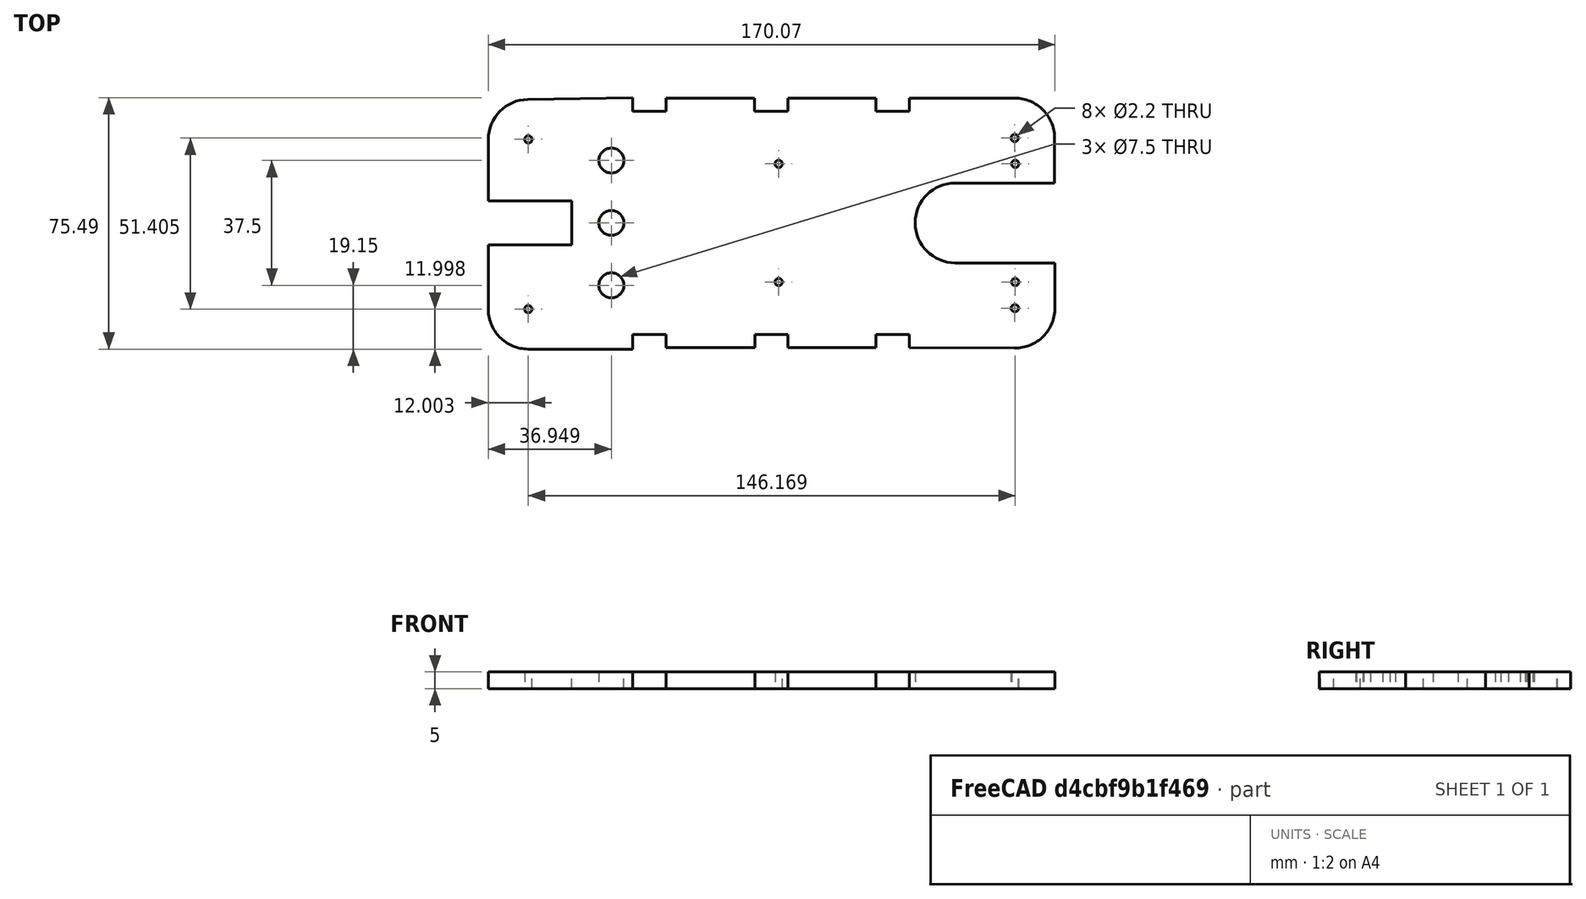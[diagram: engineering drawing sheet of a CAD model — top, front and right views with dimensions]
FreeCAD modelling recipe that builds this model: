
FCSTD DOCUMENT  (FreeCAD 1.0R38643 (Git))
Label: Acryl04
License: All rights reserved
LicenseURL: https://en.wikipedia.org/wiki/All_rights_reserved
objects: TechDraw::DrawViewDimension×26, Sketcher::SketchObject×1, PartDesign::Pad×1, PartDesign::Body×1, TechDraw::DrawSVGTemplate×1, TechDraw::DrawProjGroupItem×1, TechDraw::DrawPage×1
note: 51 computed .brp shape members not serialized (recipe doc carries the construction recipe); baked Part::Feature solids carry a one-line shape summary decoded from their .brp

FEATURE [Sketcher::SketchObject] Sketch
  ArcFitTolerance = 1e-06
  AttachmentSupport = -> [XY_Plane]
  FullyConstrained = false
  MakeInternals = false
  MapMode = 5
  sketch-geometry (59):
    g0: LineSegment StartX=-152.2 StartY=62.599 StartZ=0 EndX=-152.2 EndY=44.0923 EndZ=0
    g1: LineSegment StartX=-140.207 StartY=-0.401585 StartZ=0 EndX=-108.827 EndY=-0.401585 EndZ=0
    g2: LineSegment StartX=5.80682 StartY=75.0036 StartZ=0 EndX=-25.8266 EndY=75.0036 EndZ=0
    g3: ArcOfCircle CenterX=-140.2 CenterY=62.599 CenterZ=0 NormalX=0 NormalY=0 NormalZ=1 AngleXU=0 Radius=12 StartAngle=1.58146 EndAngle=3.14159
    g4: ArcOfCircle CenterX=-140.207 CenterY=11.5984 CenterZ=0 NormalX=0 NormalY=0 NormalZ=1 AngleXU=0 Radius=12 StartAngle=3.10801 EndAngle=4.71239
    g5: ArcOfCircle CenterX=5.86058 CenterY=11.8821 CenterZ=0 NormalX=0 NormalY=0 NormalZ=1 AngleXU=0 Radius=12 StartAngle=4.71296 EndAngle=6.29301
    g6: ArcOfCircle CenterX=5.80682 CenterY=63.0036 CenterZ=0 NormalX=0 NormalY=0 NormalZ=1 AngleXU=0 Radius=12 StartAngle=6.24947 EndAngle=7.85398
    g7: GeomPoint [constr] X=-152.2 Y=74.4139 Z=0
    g8: Circle CenterX=5.96219 CenterY=55.25 CenterZ=0 NormalX=0 NormalY=0 NormalZ=1 AngleXU=0 Radius=1.1
    g9: Circle CenterX=-65.0378 CenterY=55.25 CenterZ=0 NormalX=0 NormalY=0 NormalZ=1 AngleXU=0 Radius=1.1
    g10: Circle CenterX=-65.0378 CenterY=19.75 CenterZ=0 NormalX=0 NormalY=0 NormalZ=1 AngleXU=0 Radius=1.1
    g11: Circle CenterX=5.96219 CenterY=19.75 CenterZ=0 NormalX=0 NormalY=0 NormalZ=1 AngleXU=0 Radius=1.1
    g12: ArcOfCircle CenterX=-12.05 CenterY=37.5 CenterZ=0 NormalX=0 NormalY=0 NormalZ=1 AngleXU=0 Radius=12 StartAngle=1.5708 EndAngle=4.71239
    g13: LineSegment StartX=17.86 StartY=25.5 StartZ=0 EndX=-12.05 EndY=25.5 EndZ=0
    g14: LineSegment StartX=17.8 StartY=49.5 StartZ=0 EndX=-12.05 EndY=49.5 EndZ=0
    g15: GeomPoint X=17.8 Y=49.5 Z=0
    g16: GeomPoint X=17.86 Y=25.5 Z=0
    g17: LineSegment StartX=17.86 StartY=25.5 StartZ=0 EndX=17.86 EndY=12 EndZ=0
    g18: LineSegment StartX=17.8 StartY=49.5 StartZ=0 EndX=17.8 EndY=62.599 EndZ=0
    g19: Circle CenterX=-140.2 CenterY=62.599 CenterZ=0 NormalX=0 NormalY=0 NormalZ=1 AngleXU=0 Radius=1.1
    g20: Circle CenterX=-140.207 CenterY=11.5984 CenterZ=0 NormalX=0 NormalY=0 NormalZ=1 AngleXU=0 Radius=1.1
    g21: Circle CenterX=5.86058 CenterY=11.8821 CenterZ=0 NormalX=0 NormalY=0 NormalZ=1 AngleXU=0 Radius=1.1
    g22: Circle CenterX=5.80682 CenterY=63.0036 CenterZ=0 NormalX=0 NormalY=0 NormalZ=1 AngleXU=0 Radius=1.1
    g23: GeomPoint X=-115.261 Y=37.5 Z=0
    g24: Circle CenterX=-115.261 CenterY=37.5 CenterZ=0 NormalX=0 NormalY=0 NormalZ=1 AngleXU=0 Radius=3.75
    g25: Circle CenterX=-115.261 CenterY=56.25 CenterZ=0 NormalX=0 NormalY=0 NormalZ=1 AngleXU=0 Radius=3.75
    g26: GeomPoint X=-110.295 Y=56.25 Z=0
    g27: GeomPoint X=-115.261 Y=56.25 Z=0
    g28: Circle CenterX=-115.261 CenterY=18.75 CenterZ=0 NormalX=0 NormalY=0 NormalZ=1 AngleXU=0 Radius=3.75
    g29: GeomPoint X=-115.261 Y=18.75 Z=0
    g30: LineSegment StartX=-108.82 StartY=71.0877 StartZ=0 EndX=-98.82 EndY=71.0877 EndZ=0
    g31: LineSegment StartX=-72.3266 StartY=71 StartZ=0 EndX=-62.3266 EndY=71 EndZ=0
    g32: LineSegment StartX=-62.3266 StartY=71 StartZ=0 EndX=-62.3266 EndY=75 EndZ=0
    g33: LineSegment StartX=-72.3266 StartY=75 StartZ=0 EndX=-72.3266 EndY=71 EndZ=0
    g34: LineSegment StartX=-35.8266 StartY=71 StartZ=0 EndX=-25.8266 EndY=71 EndZ=0
    g35: LineSegment StartX=-25.8266 StartY=71 StartZ=0 EndX=-25.8266 EndY=75.0036 EndZ=0
    g36: LineSegment StartX=-35.8266 StartY=75 StartZ=0 EndX=-35.8266 EndY=71 EndZ=0
    g37: GeomPoint X=-108.82 Y=75.0877 Z=0
    g38: LineSegment StartX=-108.82 StartY=75.0877 StartZ=0 EndX=-108.82 EndY=71.0877 EndZ=0
    g39: LineSegment StartX=-98.82 StartY=71.0877 StartZ=0 EndX=-98.82 EndY=75 EndZ=0
    g40: LineSegment StartX=-108.82 StartY=75.0877 StartZ=0 EndX=-140.328 EndY=74.5983 EndZ=0
    g41: LineSegment StartX=-72.3266 StartY=75 StartZ=0 EndX=-98.82 EndY=75 EndZ=0
    g42: LineSegment StartX=-35.8266 StartY=75 StartZ=0 EndX=-62.3266 EndY=75 EndZ=0
    g43: LineSegment StartX=-98.8266 StartY=0 StartZ=0 EndX=-98.8266 EndY=4 EndZ=0
    g44: LineSegment StartX=-98.8266 StartY=4 StartZ=0 EndX=-108.827 EndY=4 EndZ=0
    g45: LineSegment StartX=-108.827 StartY=4 StartZ=0 EndX=-108.827 EndY=-0.401585 EndZ=0
    g46: LineSegment StartX=-62.2333 StartY=0 StartZ=0 EndX=-62.2333 EndY=4 EndZ=0
    g47: LineSegment StartX=-62.2333 StartY=4 StartZ=0 EndX=-72.2333 EndY=4 EndZ=0
    g48: LineSegment StartX=-72.2333 StartY=4 StartZ=0 EndX=-72.2333 EndY=0 EndZ=0
    g49: LineSegment StartX=-25.8266 StartY=0 StartZ=0 EndX=-25.8266 EndY=4 EndZ=0
    g50: LineSegment StartX=-25.8266 StartY=4 StartZ=0 EndX=-35.8266 EndY=4 EndZ=0
    g51: LineSegment StartX=-35.8266 StartY=4 StartZ=0 EndX=-35.8266 EndY=4e-16 EndZ=0
    g52: LineSegment StartX=-62.2333 StartY=0 StartZ=0 EndX=-35.8266 EndY=5e-16 EndZ=0
    g53: LineSegment StartX=-98.8266 StartY=0 StartZ=0 EndX=-72.2333 EndY=0 EndZ=0
    g54: LineSegment StartX=-25.8266 StartY=0 StartZ=0 EndX=5.86745 EndY=-0.117862 EndZ=0
    g55: LineSegment StartX=-152.2 StartY=30.8923 StartZ=0 EndX=-127.2 EndY=30.8923 EndZ=0
    g56: LineSegment StartX=-127.2 StartY=30.8923 StartZ=0 EndX=-127.2 EndY=44.0923 EndZ=0
    g57: LineSegment StartX=-127.2 StartY=44.0923 StartZ=0 EndX=-152.2 EndY=44.0923 EndZ=0
    g58: LineSegment StartX=-152.2 StartY=30.8923 StartZ=0 EndX=-152.2 EndY=12.0013 EndZ=0
  constraints (120):
    c: Tangent(g0,g3) = -1.5708
    c: Coincident(g58,g4) = -1.5708
    c: Tangent(g1,g4) = -1.5708
    c: Coincident(g54,g5) = -1.5708
    c: Tangent(g2,g6) = -1.5708
    c: Coincident(g40,g3) = -1.5708
    c: Vertical(g0)
    c: Horizontal(g1)
    c: Horizontal(g2)
    c: Equal(g3,g4)
    c: Equal(g4,g5)
    c: Equal(g5,g6)
    c: PointOnObject(g7,g0)
    c: PointOnObject(g7,g40)
    c: Distance(g0,g6) = 170
    c: Distance(g1,g40) = 75
    c: Radius(g4) = 12
    c: Diameter(g8) = 2.2
    c: Diameter(g9) = 2.2
    c: Horizontal(g8,g9)
    c: DistanceX(g9,g8) = 71
    c: Diameter(g10) = 2.2
    c: Diameter(g11) = 2.2
    c: Vertical(g10,g9)
    c: Vertical(g11,g8)
    c: Horizontal(g10,g11)
    c: DistanceY(g10,g9) = 35.5
    c: Tangent(g12,g13) = 1.5708
    c: Tangent(g12,g14) = -1.5708
    c: Angle(g-1,g13) = 3.14159
    c: Coincident(g15,g14)
    c: Coincident(g16,g13)
    c: Coincident(g17,g13)
    c: Vertical(g17)
    c: Coincident(g18,g14)
    c: Vertical(g18)
    c: Diameter(g19) = 2.2
    c: Coincident(g19,g3)
    c: Diameter(g20) = 2.2
    c: Coincident(g20,g4)
    c: Diameter(g21) = 2.2
    c: Coincident(g21,g5)
    c: Diameter(g22) = 2.2
    c: Coincident(g22,g6)
    c: Diameter(g24) = 7.5
    c: Coincident(g24,g23)
    c: Diameter(g25) = 7.5
    c: Coincident(g25,g27)
    c: Diameter(g28) = 7.5
    c: Coincident(g29,g28)
    c: Horizontal(g30)
    c: Distance(g30,g30) = 10
    c: Coincident(g31,g32)
    c: Coincident(g33,g31)
    c: Horizontal(g31)
    c: Vertical(g32)
    c: Vertical(g33)
    c: Distance(g32,g33) = 10
    c: Coincident(g34,g35)
    c: Coincident(g36,g34)
    c: Horizontal(g34)
    c: Vertical(g35)
    c: Vertical(g36)
    c: Distance(g35,g36) = 10
    c: Coincident(g38,g37)
    c: Coincident(g38,g30)
    c: Vertical(g38)
    c: Coincident(g39,g30)
    c: Vertical(g39)
    c: Coincident(g41,g39)
    c: PointOnObject(g33,g41)
    c: Coincident(g42,g32)
    c: PointOnObject(g41,g33)
    c: PointOnObject(g36,g42)
    c: Coincident(g2,g35)
    c: PointOnObject(g42,g36)
    c: Coincident(g43,g44)
    c: Coincident(g44,g45)
    c: Horizontal(g44)
    c: Vertical(g43)
    c: Vertical(g45)
    c: Coincident(g46,g47)
    c: Coincident(g47,g48)
    c: Horizontal(g47)
    c: Vertical(g46)
    c: Vertical(g48)
    c: Coincident(g49,g50)
    c: Coincident(g50,g51)
    c: Horizontal(g50)
    c: Vertical(g49)
    c: Vertical(g51)
    c: PointOnObject(g43,g53)
    c: PointOnObject(g46,g52)
    c: Coincident(g53,g48)
    c: PointOnObject(g52,g46)
    c: Coincident(g1,g45)
    c: PointOnObject(g53,g43)
    c: Coincident(g52,g51)
    c: Coincident(g49,g54)
    c: Coincident(g55,g56)
    c: Coincident(g56,g57)
    c: Horizontal(g55)
    c: Horizontal(g57)
    c: Vertical(g56)
    c: Distance(g56,g55) = 25
    c: Distance(g55,g57) = 13.2
    c: Coincident(g6,g18)
    c: Coincident(g57,g0)
    c: DistanceX(g0,g12) = 140.15
    c: Vertical(g58,g0)
    c: Coincident(g58,g55)
    c: DistanceX(g12,g17) = 29.91
    c: DistanceY(g17,g12) = 25.5
    c: Coincident(g17,g5)
    c: DistanceX(g40,g12) = 96.77
    c: DistanceX(g0,g6) = 170
    c: Vertical(g55,g4)
    c: DistanceX(g12,g-1) = 12.05
    c: DistanceY(g30,g37) = 4
    c: Coincident(g40,g37)
FEATURE [PartDesign::Pad] Pad
  Direction = (0,0,1)
  Length = 5
  Length2 = 10
  Profile = -> Sketch
  ReferenceAxis = -> Sketch [N_Axis]
  Refine = true
  Suppressed = false
  Type = 0
FEATURE [PartDesign::Body] Body
  AllowCompound = false
  Group = -> [Sketch,Pad]
  Origin = -> Origin
  Tip = -> Pad
FEATURE [TechDraw::DrawSVGTemplate] Template
  Height = 210
  Orientation = 1
  Template = <path>
  Width = 297
FEATURE [TechDraw::DrawProjGroupItem] View
  CoarseView = false
  Direction = (0,0,1)
  Focus = 100
  HardHidden = false
  IsoCount = 0
  IsoHidden = false
  IsoVisible = false
  LockPosition = false
  Perspective = false
  Rotation = 0
  RotationVector = (1,0,0)
  ScaleType = 0
  ScrubCount = 1
  SeamHidden = false
  SeamVisible = false
  SmoothHidden = false
  SmoothVisible = true
  Source = -> [Body]
  Type = 0
  X = 146.213
  XDirection = (1,0,0)
  Y = 105.457
FEATURE [TechDraw::DrawViewDimension] Dimension
  AngleOverride = false
  Arbitrary = false
  ArbitraryTolerances = false
  BoxCorners = (2) [(-85.0337,-37.7447,0),(85.0337,37.7447,0)]
  EqualTolerance = true
  ExtensionAngle = 0
  FormatSpec = %.2w
  FormatSpecOverTolerance = %+.2w
  FormatSpecUnderTolerance = %+.2w
  Inverted = false
  LineAngle = 0
  LockPosition = false
  MeasureType = 1
  OverTolerance = 0
  References2D = -> [View]
  Rotation = 0
  ScaleType = 0
  TheoreticalExact = false
  Type = 1
  UnderTolerance = 0
  X = -36.6469
  Y = 49.1205
FEATURE [TechDraw::DrawViewDimension] Dimension001
  AngleOverride = false
  Arbitrary = false
  ArbitraryTolerances = false
  BoxCorners = (2) [(-85.0337,-37.7447,0),(85.0337,37.7447,0)]
  EqualTolerance = true
  ExtensionAngle = 0
  FormatSpec = %.2w
  FormatSpecOverTolerance = %+.2w
  FormatSpecUnderTolerance = %+.2w
  Inverted = false
  LineAngle = 0
  LockPosition = false
  MeasureType = 1
  OverTolerance = 0
  References2D = -> [View]
  Rotation = 0
  ScaleType = 0
  TheoreticalExact = false
  Type = 2
  UnderTolerance = 0
  X = 10.1068
  Y = 35.6569
FEATURE [TechDraw::DrawViewDimension] Dimension002
  AngleOverride = false
  Arbitrary = false
  ArbitraryTolerances = false
  BoxCorners = (2) [(-85.0337,-37.7447,0),(85.0337,37.7447,0)]
  EqualTolerance = true
  ExtensionAngle = 0
  FormatSpec = %.2w
  FormatSpecOverTolerance = %+.2w
  FormatSpecUnderTolerance = %+.2w
  Inverted = false
  LineAngle = 0
  LockPosition = false
  MeasureType = 1
  OverTolerance = 0
  References2D = -> [View]
  Rotation = 0
  ScaleType = 0
  TheoreticalExact = false
  Type = 1
  UnderTolerance = 0
  X = -4.82983
  Y = 57.9458
FEATURE [TechDraw::DrawViewDimension] Dimension003
  AngleOverride = false
  Arbitrary = false
  ArbitraryTolerances = false
  BoxCorners = (2) [(-85.0337,-37.7447,0),(85.0337,37.7447,0)]
  EqualTolerance = true
  ExtensionAngle = 0
  FormatSpec = %.2w
  FormatSpecOverTolerance = %+.2w
  FormatSpecUnderTolerance = %+.2w
  Inverted = false
  LineAngle = 0
  LockPosition = false
  MeasureType = 1
  OverTolerance = 0
  References2D = -> [View]
  Rotation = 0
  ScaleType = 0
  TheoreticalExact = false
  Type = 2
  UnderTolerance = 0
  X = 93.5942
  Y = 0.099765
FEATURE [TechDraw::DrawViewDimension] Dimension004
  AngleOverride = false
  Arbitrary = false
  ArbitraryTolerances = false
  BoxCorners = (2) [(-85.0337,-37.7447,0),(85.0337,37.7447,0)]
  EqualTolerance = true
  ExtensionAngle = 0
  FormatSpec = %.2w
  FormatSpecOverTolerance = %+.2w
  FormatSpecUnderTolerance = %+.2w
  Inverted = false
  LineAngle = 0
  LockPosition = false
  MeasureType = 1
  OverTolerance = 0
  References2D = -> [View]
  Rotation = 0
  ScaleType = 0
  TheoreticalExact = false
  Type = 1
  UnderTolerance = 0
  X = -72.5269
  Y = 14.7383
FEATURE [TechDraw::DrawViewDimension] Dimension005
  AngleOverride = false
  Arbitrary = false
  ArbitraryTolerances = false
  BoxCorners = (2) [(-85.0337,-37.7447,0),(85.0337,37.7447,0)]
  EqualTolerance = true
  ExtensionAngle = 0
  FormatSpec = %.2w
  FormatSpecOverTolerance = %+.2w
  FormatSpecUnderTolerance = %+.2w
  Inverted = false
  LineAngle = 0
  LockPosition = false
  MeasureType = 1
  OverTolerance = 0
  References2D = -> [View]
  Rotation = 0
  ScaleType = 0
  TheoreticalExact = false
  Type = 1
  UnderTolerance = 0
  X = -54.0575
  Y = -25.8768
FEATURE [TechDraw::DrawViewDimension] Dimension006
  AngleOverride = false
  Arbitrary = false
  ArbitraryTolerances = false
  BoxCorners = (2) [(-85.0337,-37.7447,0),(85.0337,37.7447,0)]
  EqualTolerance = true
  ExtensionAngle = 0
  FormatSpec = %.2w
  FormatSpecOverTolerance = %+.2w
  FormatSpecUnderTolerance = %+.2w
  Inverted = false
  LineAngle = 0
  LockPosition = false
  MeasureType = 1
  OverTolerance = 0
  References2D = -> [View]
  Rotation = 0
  ScaleType = 0
  TheoreticalExact = false
  Type = 1
  UnderTolerance = 0
  X = -22.9764
  Y = 11.5319
FEATURE [TechDraw::DrawViewDimension] Dimension007
  AngleOverride = false
  Arbitrary = false
  ArbitraryTolerances = false
  BoxCorners = (2) [(-85.0337,-37.7447,0),(85.0337,37.7447,0)]
  EqualTolerance = true
  ExtensionAngle = 0
  FormatSpec = %.2w
  FormatSpecOverTolerance = %+.2w
  FormatSpecUnderTolerance = %+.2w
  Inverted = false
  LineAngle = 0
  LockPosition = false
  MeasureType = 1
  OverTolerance = 0
  References2D = -> [View]
  Rotation = 0
  ScaleType = 0
  TheoreticalExact = false
  Type = 1
  UnderTolerance = 0
  X = 70.0481
  Y = 7.73832
FEATURE [TechDraw::DrawViewDimension] Dimension008
  AngleOverride = false
  Arbitrary = false
  ArbitraryTolerances = false
  BoxCorners = (2) [(-85.0337,-37.7447,0),(85.0337,37.7447,0)]
  EqualTolerance = true
  ExtensionAngle = 0
  FormatSpec = %.2w
  FormatSpecOverTolerance = %+.2w
  FormatSpecUnderTolerance = %+.2w
  Inverted = false
  LineAngle = 0
  LockPosition = false
  MeasureType = 1
  OverTolerance = 0
  References2D = -> [View]
  Rotation = 0
  ScaleType = 0
  TheoreticalExact = false
  Type = 1
  UnderTolerance = 0
  X = 78.9765
  Y = 47.4304
FEATURE [TechDraw::DrawViewDimension] Dimension009
  AngleOverride = false
  Arbitrary = false
  ArbitraryTolerances = false
  BoxCorners = (2) [(-85.0337,-37.7447,0),(85.0337,37.7447,0)]
  EqualTolerance = true
  ExtensionAngle = 0
  FormatSpec = %.2w
  FormatSpecOverTolerance = %+.2w
  FormatSpecUnderTolerance = %+.2w
  Inverted = false
  LineAngle = 0
  LockPosition = false
  MeasureType = 1
  OverTolerance = 0
  References2D = -> [View]
  Rotation = 0
  ScaleType = 0
  TheoreticalExact = false
  Type = 2
  UnderTolerance = 0
  X = 56.933
  Y = 21.7837
FEATURE [TechDraw::DrawViewDimension] Dimension010
  AngleOverride = false
  Arbitrary = false
  ArbitraryTolerances = false
  BoxCorners = (2) [(-85.0337,-37.7447,0),(85.0337,37.7447,0)]
  EqualTolerance = true
  ExtensionAngle = 0
  FormatSpec = %.2w
  FormatSpecOverTolerance = %+.2w
  FormatSpecUnderTolerance = %+.2w
  Inverted = false
  LineAngle = 0
  LockPosition = false
  MeasureType = 1
  OverTolerance = 0
  References2D = -> [View]
  Rotation = 0
  ScaleType = 0
  TheoreticalExact = false
  Type = 2
  UnderTolerance = 0
  X = -15.9972
  Y = 25.7819
FEATURE [TechDraw::DrawViewDimension] Dimension011
  AngleOverride = false
  Arbitrary = false
  ArbitraryTolerances = false
  BoxCorners = (2) [(-85.0337,-37.7447,0),(85.0337,37.7447,0)]
  EqualTolerance = true
  ExtensionAngle = 0
  FormatSpec = %.2w
  FormatSpecOverTolerance = %+.2w
  FormatSpecUnderTolerance = %+.2w
  Inverted = false
  LineAngle = 0
  LockPosition = false
  MeasureType = 1
  OverTolerance = 0
  References2D = -> [View]
  Rotation = 0
  ScaleType = 0
  TheoreticalExact = false
  Type = 2
  UnderTolerance = 0
  X = 10.1068
  Y = -25.4681
FEATURE [TechDraw::DrawViewDimension] Dimension012
  AngleOverride = false
  Arbitrary = false
  ArbitraryTolerances = false
  BoxCorners = (2) [(-85.0337,-37.7447,0),(85.0337,37.7447,0)]
  EqualTolerance = true
  ExtensionAngle = 0
  FormatSpec = %.2w
  FormatSpecOverTolerance = %+.2w
  FormatSpecUnderTolerance = %+.2w
  Inverted = false
  LineAngle = 0
  LockPosition = false
  MeasureType = 1
  OverTolerance = 0
  References2D = -> [View]
  Rotation = 0
  ScaleType = 0
  TheoreticalExact = false
  Type = 2
  UnderTolerance = 0
  X = 102.236
  Y = 0.156918
FEATURE [TechDraw::DrawViewDimension] Dimension013
  AngleOverride = false
  Arbitrary = false
  ArbitraryTolerances = false
  BoxCorners = (2) [(-85.0337,-37.7447,0),(85.0337,37.7447,0)]
  EqualTolerance = true
  ExtensionAngle = 0
  FormatSpec = %.2w
  FormatSpecOverTolerance = %+.2w
  FormatSpecUnderTolerance = %+.2w
  Inverted = false
  LineAngle = 0
  LockPosition = false
  MeasureType = 1
  OverTolerance = 0
  References2D = -> [View]
  Rotation = 0
  ScaleType = 0
  TheoreticalExact = false
  Type = 2
  UnderTolerance = 0
  X = 76.167
  Y = 31.6605
FEATURE [TechDraw::DrawViewDimension] Dimension014
  AngleOverride = false
  Arbitrary = false
  ArbitraryTolerances = false
  BoxCorners = (2) [(-85.0337,-37.7447,0),(85.0337,37.7447,0)]
  EqualTolerance = true
  ExtensionAngle = 0
  FormatSpec = %.2w
  FormatSpecOverTolerance = %+.2w
  FormatSpecUnderTolerance = %+.2w
  Inverted = false
  LineAngle = 0
  LockPosition = false
  MeasureType = 1
  OverTolerance = 0
  References2D = -> [View]
  Rotation = 0
  ScaleType = 0
  TheoreticalExact = false
  Type = 1
  UnderTolerance = 0
  X = -63.3369
  Y = 47.4304
FEATURE [TechDraw::DrawViewDimension] Dimension015
  AngleOverride = false
  Arbitrary = false
  ArbitraryTolerances = false
  BoxCorners = (2) [(-85.0337,-37.7447,0),(85.0337,37.7447,0)]
  EqualTolerance = true
  ExtensionAngle = 0
  FormatSpec = %.2w
  FormatSpecOverTolerance = %+.2w
  FormatSpecUnderTolerance = %+.2w
  Inverted = false
  LineAngle = 0
  LockPosition = false
  MeasureType = 1
  OverTolerance = 0
  References2D = -> [View]
  Rotation = 0
  ScaleType = 0
  TheoreticalExact = false
  Type = 1
  UnderTolerance = 0
  X = -18.4002
  Y = 47.4304
FEATURE [TechDraw::DrawViewDimension] Dimension016
  AngleOverride = false
  Arbitrary = false
  ArbitraryTolerances = false
  BoxCorners = (2) [(-85.0337,-37.7447,0),(85.0337,37.7447,0)]
  EqualTolerance = true
  ExtensionAngle = 0
  FormatSpec = %.2w
  FormatSpecOverTolerance = %+.2w
  FormatSpecUnderTolerance = %+.2w
  Inverted = false
  LineAngle = 0
  LockPosition = false
  MeasureType = 1
  OverTolerance = 0
  References2D = -> [View]
  Rotation = 0
  ScaleType = 0
  TheoreticalExact = false
  Type = 1
  UnderTolerance = 0
  X = 18.0965
  Y = 49.1205
FEATURE [TechDraw::DrawViewDimension] Dimension017
  AngleOverride = false
  Arbitrary = false
  ArbitraryTolerances = false
  BoxCorners = (2) [(-85.0337,-37.7447,0),(85.0337,37.7447,0)]
  EqualTolerance = true
  ExtensionAngle = 0
  FormatSpec = %.2w
  FormatSpecOverTolerance = %+.2w
  FormatSpecUnderTolerance = %+.2w
  Inverted = false
  LineAngle = 0
  LockPosition = false
  MeasureType = 1
  OverTolerance = 0
  References2D = -> [View]
  Rotation = 0
  ScaleType = 0
  TheoreticalExact = false
  Type = 2
  UnderTolerance = 0
  X = -94.2844
  Y = 0.149259
FEATURE [TechDraw::DrawViewDimension] Dimension018
  AngleOverride = false
  Arbitrary = false
  ArbitraryTolerances = false
  BoxCorners = (2) [(-85.0337,-37.7447,0),(85.0337,37.7447,0)]
  EqualTolerance = true
  ExtensionAngle = 0
  FormatSpec = %.2w
  FormatSpecOverTolerance = %+.2w
  FormatSpecUnderTolerance = %+.2w
  Inverted = false
  LineAngle = 0
  LockPosition = false
  MeasureType = 1
  OverTolerance = 0
  References2D = -> [View]
  Rotation = 0
  ScaleType = 0
  TheoreticalExact = false
  Type = 2
  UnderTolerance = 0
  X = -35.4019
  Y = -9.21808
FEATURE [TechDraw::DrawViewDimension] Dimension019
  AngleOverride = false
  Arbitrary = false
  ArbitraryTolerances = false
  BoxCorners = (2) [(-85.0337,-37.7447,0),(85.0337,37.7447,0)]
  EqualTolerance = true
  ExtensionAngle = 0
  FormatSpec = ⌀%.2w
  FormatSpecOverTolerance = %+.2w
  FormatSpecUnderTolerance = %+.2w
  Inverted = false
  LineAngle = 0
  LockPosition = false
  MeasureType = 1
  OverTolerance = 0
  References2D = -> [View]
  Rotation = 0
  ScaleType = 0
  TheoreticalExact = false
  Type = 5
  UnderTolerance = 0
  X = -54.3844
  Y = 29.582
FEATURE [TechDraw::DrawViewDimension] Dimension020
  AngleOverride = false
  Arbitrary = false
  ArbitraryTolerances = false
  BoxCorners = (2) [(-85.0337,-37.7447,0),(85.0337,37.7447,0)]
  EqualTolerance = true
  ExtensionAngle = 0
  FormatSpec = ⌀%.2w
  FormatSpecOverTolerance = %+.2w
  FormatSpecUnderTolerance = %+.2w
  Inverted = false
  LineAngle = 0
  LockPosition = false
  MeasureType = 1
  OverTolerance = 0
  References2D = -> [View]
  Rotation = 0
  ScaleType = 0
  TheoreticalExact = false
  Type = 5
  UnderTolerance = 0
  X = 15.1278
  Y = 14.211
FEATURE [TechDraw::DrawViewDimension] Dimension021
  AngleOverride = false
  Arbitrary = false
  ArbitraryTolerances = false
  BoxCorners = (2) [(-85.0337,-37.7447,0),(85.0337,37.7447,0)]
  EqualTolerance = true
  ExtensionAngle = 0
  FormatSpec = ⌀%.2w
  FormatSpecOverTolerance = %+.2w
  FormatSpecUnderTolerance = %+.2w
  Inverted = false
  LineAngle = 0
  LockPosition = false
  MeasureType = 1
  OverTolerance = 0
  References2D = -> [View]
  Rotation = 0
  ScaleType = 0
  TheoreticalExact = false
  Type = 5
  UnderTolerance = 0
  X = 1.23689
  Y = -5.50976
FEATURE [TechDraw::DrawViewDimension] Dimension022
  AngleOverride = false
  Arbitrary = false
  ArbitraryTolerances = false
  BoxCorners = (2) [(-85.0337,-37.7447,0),(85.0337,37.7447,0)]
  EqualTolerance = true
  ExtensionAngle = 0
  FormatSpec = ⌀%.2w
  FormatSpecOverTolerance = %+.2w
  FormatSpecUnderTolerance = %+.2w
  Inverted = false
  LineAngle = 0
  LockPosition = false
  MeasureType = 1
  OverTolerance = 0
  References2D = -> [View]
  Rotation = 0
  ScaleType = 0
  TheoreticalExact = false
  Type = 5
  UnderTolerance = 0
  X = 60.3223
  Y = -16.6003
FEATURE [TechDraw::DrawViewDimension] Dimension023
  AngleOverride = false
  Arbitrary = false
  ArbitraryTolerances = false
  BoxCorners = (2) [(-85.0337,-37.7447,0),(85.0337,37.7447,0)]
  EqualTolerance = true
  ExtensionAngle = 0
  FormatSpec = ⌀%.2w
  FormatSpecOverTolerance = %+.2w
  FormatSpecUnderTolerance = %+.2w
  Inverted = false
  LineAngle = 0
  LockPosition = false
  MeasureType = 1
  OverTolerance = 0
  References2D = -> [View]
  Rotation = 0
  ScaleType = 0
  TheoreticalExact = false
  Type = 5
  UnderTolerance = 0
  X = 59.9007
  Y = -28.1886
FEATURE [TechDraw::DrawViewDimension] Dimension024
  AngleOverride = false
  Arbitrary = false
  ArbitraryTolerances = false
  BoxCorners = (2) [(-85.0337,-37.7447,0),(85.0337,37.7447,0)]
  EqualTolerance = true
  ExtensionAngle = 0
  FormatSpec = ⌀%.2w
  FormatSpecOverTolerance = %+.2w
  FormatSpecUnderTolerance = %+.2w
  Inverted = false
  LineAngle = 0
  LockPosition = false
  MeasureType = 1
  OverTolerance = 0
  References2D = -> [View]
  Rotation = 0
  ScaleType = 0
  TheoreticalExact = false
  Type = 5
  UnderTolerance = 0
  X = -71.4276
  Y = -16.794
FEATURE [TechDraw::DrawViewDimension] Dimension025
  AngleOverride = false
  Arbitrary = false
  ArbitraryTolerances = false
  BoxCorners = (2) [(-85.0337,-37.7447,0),(85.0337,37.7447,0)]
  EqualTolerance = true
  ExtensionAngle = 0
  FormatSpec = ⌀%.2w
  FormatSpecOverTolerance = %+.2w
  FormatSpecUnderTolerance = %+.2w
  Inverted = false
  LineAngle = 0
  LockPosition = false
  MeasureType = 1
  OverTolerance = 0
  References2D = -> [View]
  Rotation = 0
  ScaleType = 0
  TheoreticalExact = false
  Type = 5
  UnderTolerance = 0
  X = -64.1366
  Y = 22.7694
FEATURE [TechDraw::DrawPage] Page
  KeepUpdated = true
  NextBalloonIndex = 1
  ProjectionType = 0
  Template = -> Template
  Views = -> [View,Dimension,Dimension001,Dimension002,Dimension003,Dimension004,Dimension005,Dimension006,Dimension007,Dimension008,Dimension009,Dimension010,Dimension011,Dimension012,Dimension013,Dimension014,Dimension015,Dimension016,Dimension017,Dimension018,Dimension019,Dimension020,Dimension021,Dimension022,Dimension023,Dimension024,Dimension025]
note: 1 file-system path scrubbed to <path> (originals preserved in the JSON sidecar)
